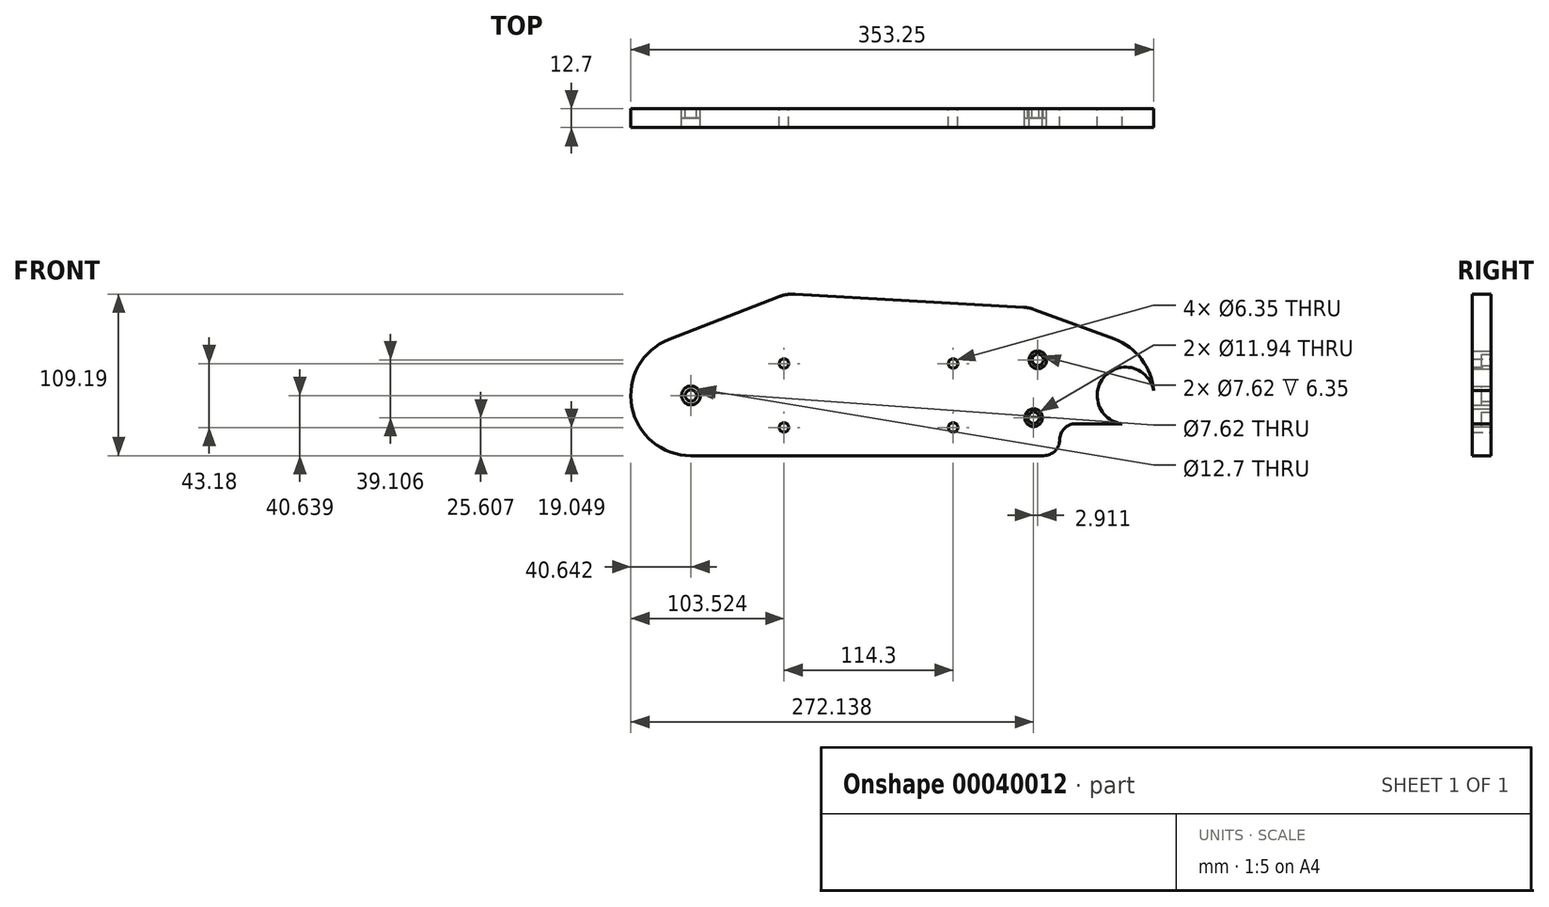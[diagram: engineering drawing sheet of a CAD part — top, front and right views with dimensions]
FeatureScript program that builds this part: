
annotation { "Feature Type Name" : "Feature", "Feature Type Description" : "" }
export const myFeature = defineFeature(function(context is Context, id is Id, definition is map)
    precondition{}
    {
        {
            var Q0;
            Q0=qCreatedBy(makeId("Front.planeOp"),FACE);
            var sketch = newSketch(context, id + "F0", { "sketchPlane" : qUnion([Q0])});
            skArc(sketch, "E0", {"start": v(-26.83, 17.95) * mm, "mid": v(-26.72, 17.95) * mm, "end": v(-26.62, 17.95) * mm});
            skArc(sketch, "E1.cCircle", {"start": v(-26.83, 17.95) * mm, "mid": v(-26.72, 17.95) * mm, "end": v(-26.62, 17.95) * mm, "construction": true});
            skLineSegment(sketch, "E2.trimOffspring", {"start": v(-26.62, 18.06) * mm, "end": v(-26.83, 17.95) * mm});
            skLineSegment(sketch, "E3.trimOffspring", {"start": v(-26.62, 18.06) * mm, "end": v(-26.62, 17.95) * mm});
            skArc(sketch, "E4", {"start": v(-168.1, -131.93) * mm, "mid": v(-168, -131.93) * mm, "end": v(-167.9, -131.93) * mm});
            skArc(sketch, "E5.cCircle", {"start": v(-168.1, -131.93) * mm, "mid": v(-168, -131.93) * mm, "end": v(-167.9, -131.93) * mm, "construction": true});
            skLineSegment(sketch, "E6.trimOffspring", {"start": v(-167.9, -131.8) * mm, "end": v(-167.9, -131.93) * mm});
            skCircle(sketch, "E7", {"center": v(-213.47, 68.19) * mm, "radius": 3.18 * mm});
            skPoint(sketch, "E8.visualSharp", {"position": v(-325.8, 115.42) * mm});
            skLineSegment(sketch, "E9", {"start": v(-158.5, 104.66) * mm, "end": v(-104.48, 84.73) * mm});
            skLineSegment(sketch, "E10", {"start": v(-330.94, 113.42) * mm, "end": v(-405.38, 84.48) * mm});
            skPoint(sketch, "E11.visualSharp", {"position": v(-98.55, 87.24) * mm});
            skPoint(sketch, "E12", {"position": v(-98.55, 65.65) * mm});
            skCircle(sketch, "E13", {"center": v(-156.24, 70.67) * mm, "radius": 5.97 * mm});
            skPoint(sketch, "E14", {"position": v(-98.55, 27.55) * mm});
            skArc(sketch, "E15.filletArc", {"start": v(-130.62, 27.55) * mm, "mid": v(-138.25, 24.39) * mm, "end": v(-141.41, 16.75) * mm});
            skPoint(sketch, "E16.visualSharp", {"position": v(-141.41, 5.96) * mm});
            skPoint(sketch, "E17.visualSharp", {"position": v(-117.28, 87.24) * mm});
            skPoint(sketch, "E15.visualSharp", {"position": v(-141.41, 27.55) * mm});
            skPoint(sketch, "E18.visualSharp", {"position": v(-138.85, 5.96) * mm});
            skPoint(sketch, "E19.visualSharp", {"position": v(-114.91, 65.65) * mm});
            skLineSegment(sketch, "E20.top", {"start": v(-390.65, 5.96) * mm, "end": v(-152.2, 5.96) * mm});
            skCircle(sketch, "E21", {"center": v(-213.47, 25) * mm, "radius": 3.18 * mm});
            skCircle(sketch, "E22", {"center": v(-327.77, 25) * mm, "radius": 3.18 * mm});
            skPoint(sketch, "E23", {"position": v(-274.52, 116.58) * mm});
            skLineSegment(sketch, "E24", {"start": v(-141.41, 27.55) * mm, "end": v(-98.55, 27.55) * mm});
            skPoint(sketch, "E25", {"position": v(-96.96, 5.96) * mm});
            skCircle(sketch, "E26", {"center": v(-390.65, 46.6) * mm, "radius": 6.35 * mm});
            skPoint(sketch, "E27", {"position": v(-77.91, 87.3) * mm});
            skArc(sketch, "E16.filletArc", {"start": v(-152.2, 5.96) * mm, "mid": v(-144.57, 9.12) * mm, "end": v(-141.41, 16.75) * mm});
            skLineSegment(sketch, "E28", {"start": v(-56.32, 56.28) * mm, "end": v(-56.32, 56.28) * mm});
            skPoint(sketch, "E29.visualSharp", {"position": v(-56.32, 27.55) * mm});
            skLineSegment(sketch, "E30.trimOffspring", {"start": v(-130.62, 27.55) * mm, "end": v(-96.96, 27.55) * mm});
            skCircle(sketch, "E31", {"center": v(-327.77, 68.19) * mm, "radius": 3.18 * mm});
            skArc(sketch, "E32", {"start": v(-405.38, 84.48) * mm, "mid": v(-430.6, 39.1) * mm, "end": v(-390.65, 5.96) * mm});
            skPoint(sketch, "E33.visualSharp", {"position": v(-162.05, 105.97) * mm});
            skCircle(sketch, "E34", {"center": v(-390.65, 46.6) * mm, "radius": 3.81 * mm});
            skCircle(sketch, "E35", {"center": v(-159.15, 31.57) * mm, "radius": 5.97 * mm});
            skArc(sketch, "E36.filletArc", {"start": v(-77.91, 46.6) * mm, "mid": v(-85.2, 69.83) * mm, "end": v(-104.48, 84.73) * mm});
            skLineSegment(sketch, "E37", {"start": v(-320.27, 115.1) * mm, "end": v(-165.83, 106.19) * mm});
            skLineSegment(sketch, "E38.left", {"start": v(-77.91, 46.6) * mm, "end": v(-77.91, 46.6) * mm});
            skPoint(sketch, "E39", {"position": v(-118.7, 46.6) * mm});
            skArc(sketch, "E33.filletArc", {"start": v(-158.5, 104.66) * mm, "mid": v(-162.1, 105.7) * mm, "end": v(-165.83, 106.19) * mm});
            skLineSegment(sketch, "E40", {"start": v(-98.55, 27.55) * mm, "end": v(-141.41, 27.55) * mm});
            skLineSegment(sketch, "E41", {"start": v(-141.41, 16.75) * mm, "end": v(-141.41, 16.75) * mm});
            skPoint(sketch, "E36.visualSharp", {"position": v(-77.91, 87.24) * mm});
            skArc(sketch, "E8.filletArc", {"start": v(-320.27, 115.1) * mm, "mid": v(-325.7, 114.84) * mm, "end": v(-330.94, 113.42) * mm});
            skLineSegment(sketch, "E38.top", {"start": v(-117.28, 87.24) * mm, "end": v(-118.55, 87.24) * mm});
            skLineSegment(sketch, "E42", {"start": v(-118.55, 87.24) * mm, "end": v(-117.28, 87.24) * mm});
            skArc(sketch, "E43", {"start": v(-78.04, 49.8) * mm, "mid": v(-110.84, 59.86) * mm, "end": v(-99.3, 27.55) * mm});
            skCircle(sketch, "E44", {"center": v(-159.15, 31.57) * mm, "radius": 3.81 * mm});
            skCircle(sketch, "E45", {"center": v(-156.24, 70.67) * mm, "radius": 3.81 * mm});
            skSolve(sketch);
        }
        {
            var Q0;
            Q0=makeQuery(id+"F0.imprint","IMPRINT",FACE,{"disambiguationData":[TD([[makeQuery(id+"F0.imprint","IMPRINT",EDGE,{"derivedFrom":sQuery(id+"F0.wireOp",EDGE,"E35")}),1.0]])]});
            var Q1;
            Q1=makeQuery(id+"F0.imprint","IMPRINT",FACE,{"disambiguationData":[TD([[makeQuery(id+"F0.imprint","IMPRINT",EDGE,{"derivedFrom":sQuery(id+"F0.wireOp",EDGE,"E13")}),1.0]])]});
            var Q2;
            Q2=makeQuery(id+"F0.imprint","IMPRINT",FACE,{"disambiguationData":[TD([[makeQuery(id+"F0.imprint","IMPRINT",EDGE,{"derivedFrom":sQuery(id+"F0.wireOp",EDGE,"E26")}),1.0]])]});
            extrude(context, id + "F1", {"entities" : qUnion([Q0, Q1, Q2]), "depth" : 6.35 * mm});
        }
        {
            var Q0;
            Q0=makeQuery(id+"F0.imprint","IMPRINT",FACE,{"disambiguationData":[TD([[makeQuery(id+"F0.imprint","IMPRINT",EDGE,{"derivedFrom":sQuery(id+"F0.wireOp",EDGE,"E7")}),-1.0]])]});
            extrude(context, id + "F2", {"entities" : qUnion([Q0]), "depth" : 12.7 * mm});
        }
    });
